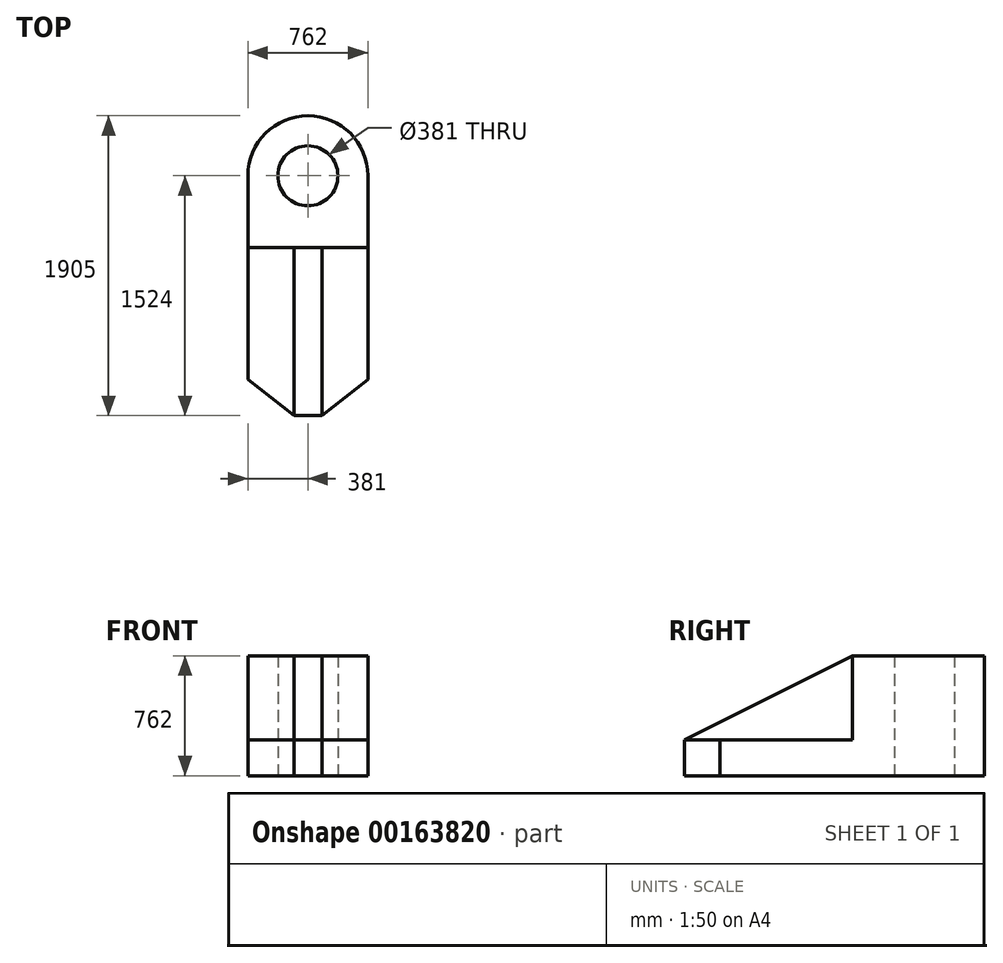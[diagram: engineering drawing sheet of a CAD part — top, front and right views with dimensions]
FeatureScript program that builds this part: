
annotation { "Feature Type Name" : "Feature", "Feature Type Description" : "" }
export const myFeature = defineFeature(function(context is Context, id is Id, definition is map)
    precondition{}
    {
        {
            var Q0;
            Q0=qCreatedBy(makeId("Top.planeOp"),FACE);
            var sketch = newSketch(context, id + "F0", { "sketchPlane" : qUnion([Q0])});
            skLineSegment(sketch, "E0", {"start": v(381, -131.9) * mm, "end": v(-381, -131.9) * mm});
            skLineSegment(sketch, "E1", {"start": v(381, -131.9) * mm, "end": v(381, 325.3) * mm});
            skLineSegment(sketch, "E2", {"start": v(-381, -131.9) * mm, "end": v(-381, 325.3) * mm});
            skArc(sketch, "E3", {"start": v(381, 325.3) * mm, "mid": v(0, 706.3) * mm, "end": v(-381, 325.3) * mm});
            skCircle(sketch, "E4", {"center": v(0, 325.3) * mm, "radius": 190.5 * mm});
            skLineSegment(sketch, "E5", {"start": v(381, -131.9) * mm, "end": v(88.9, -131.9) * mm});
            skLineSegment(sketch, "E6", {"start": v(-381, -131.9) * mm, "end": v(-88.9, -131.9) * mm});
            skLineSegment(sketch, "E7", {"start": v(-381, -131.9) * mm, "end": v(-381, -970.1) * mm});
            skLineSegment(sketch, "E8", {"start": v(381, -131.9) * mm, "end": v(381, -970.1) * mm});
            skLineSegment(sketch, "E9", {"start": v(-88.9, -131.9) * mm, "end": v(-88.9, -1198.7) * mm});
            skLineSegment(sketch, "E10", {"start": v(88.9, -131.9) * mm, "end": v(88.9, -1198.7) * mm});
            skLineSegment(sketch, "E11", {"start": v(-381, -970.1) * mm, "end": v(-88.9, -1198.7) * mm});
            skLineSegment(sketch, "E12", {"start": v(88.9, -1198.7) * mm, "end": v(-88.9, -1198.7) * mm});
            skLineSegment(sketch, "E13", {"start": v(88.9, -1198.7) * mm, "end": v(381, -970.1) * mm});
            skSolve(sketch);
        }
        {
            var Q0;
            Q0=qCreatedBy(makeId("Right.planeOp"),FACE);
            var sketch = newSketch(context, id + "F1", { "sketchPlane" : qUnion([Q0])});
            skLineSegment(sketch, "E14", {"start": v(-1196.93, 0) * mm, "end": v(-1196.93, 228.6) * mm});
            skLineSegment(sketch, "E15", {"start": v(-977.46, 0) * mm, "end": v(-977.46, 228.6) * mm});
            skLineSegment(sketch, "E16", {"start": v(-1196.93, 0) * mm, "end": v(708.07, 0) * mm});
            skLineSegment(sketch, "E17", {"start": v(-129.03, 0) * mm, "end": v(-129.03, 762) * mm});
            skLineSegment(sketch, "E18", {"start": v(-129.03, 762) * mm, "end": v(-1196.93, 228.6) * mm});
            skLineSegment(sketch, "E19", {"start": v(-1196.93, 228.6) * mm, "end": v(-977.46, 228.6) * mm});
            skLineSegment(sketch, "E20", {"start": v(-977.46, 228.6) * mm, "end": v(-129.03, 228.6) * mm});
            skSolve(sketch);
        }
        {
            var Q0;
            Q0=makeQuery(id+"F0.imprint","IMPRINT",FACE,{"disambiguationData":[TD([[makeQuery(id+"F0.imprint","IMPRINT",EDGE,{"derivedFrom":sQuery(id+"F0.wireOp",EDGE,"E0")}),-1.0]])]});
            extrude(context, id + "F2", {"entities" : qUnion([Q0]), "depth" : 762 * mm});
        }
        {
            var Q0;
            Q0=qSketchRegion(id+"F0",true);
            extrude(context, id + "F3", {"entities" : qUnion([Q0]), "operationType" : NewBodyOperationType.ADD, "depth" : 228.6 * mm});
        }
        {
            var Q0;
            {var subQ0=sQuery(id+"F1.wireOp",EDGE,"E18");Q0=makeQuery(id+"F1.imprint","IMPRINT",FACE,{"disambiguationData":[TD([[makeQuery(id+"F1.imprint","IMPRINT",EDGE,{"derivedFrom":subQ0}),1.0]])]});}
            extrude(context, id + "F4", {"entities" : qUnion([Q0]), "operationType" : NewBodyOperationType.ADD, "depth" : 88.9 * mm});
        }
        {
            var Q0;
            Q0=makeQuery(id+"F4.opExtrude","CAP_FACE",FACE,{"disambiguationData":[OSD([sQuery(id+"F1.wireOp",EDGE,"E17"),sQuery(id+"F1.wireOp",EDGE,"E18"),sQuery(id+"F1.wireOp",EDGE,"E19"),sQuery(id+"F1.wireOp",EDGE,"E20")])],"isStart":true});
            extrude(context, id + "F5", {"entities" : qUnion([Q0]), "operationType" : NewBodyOperationType.ADD, "depth" : 88.9 * mm});
        }
    });
